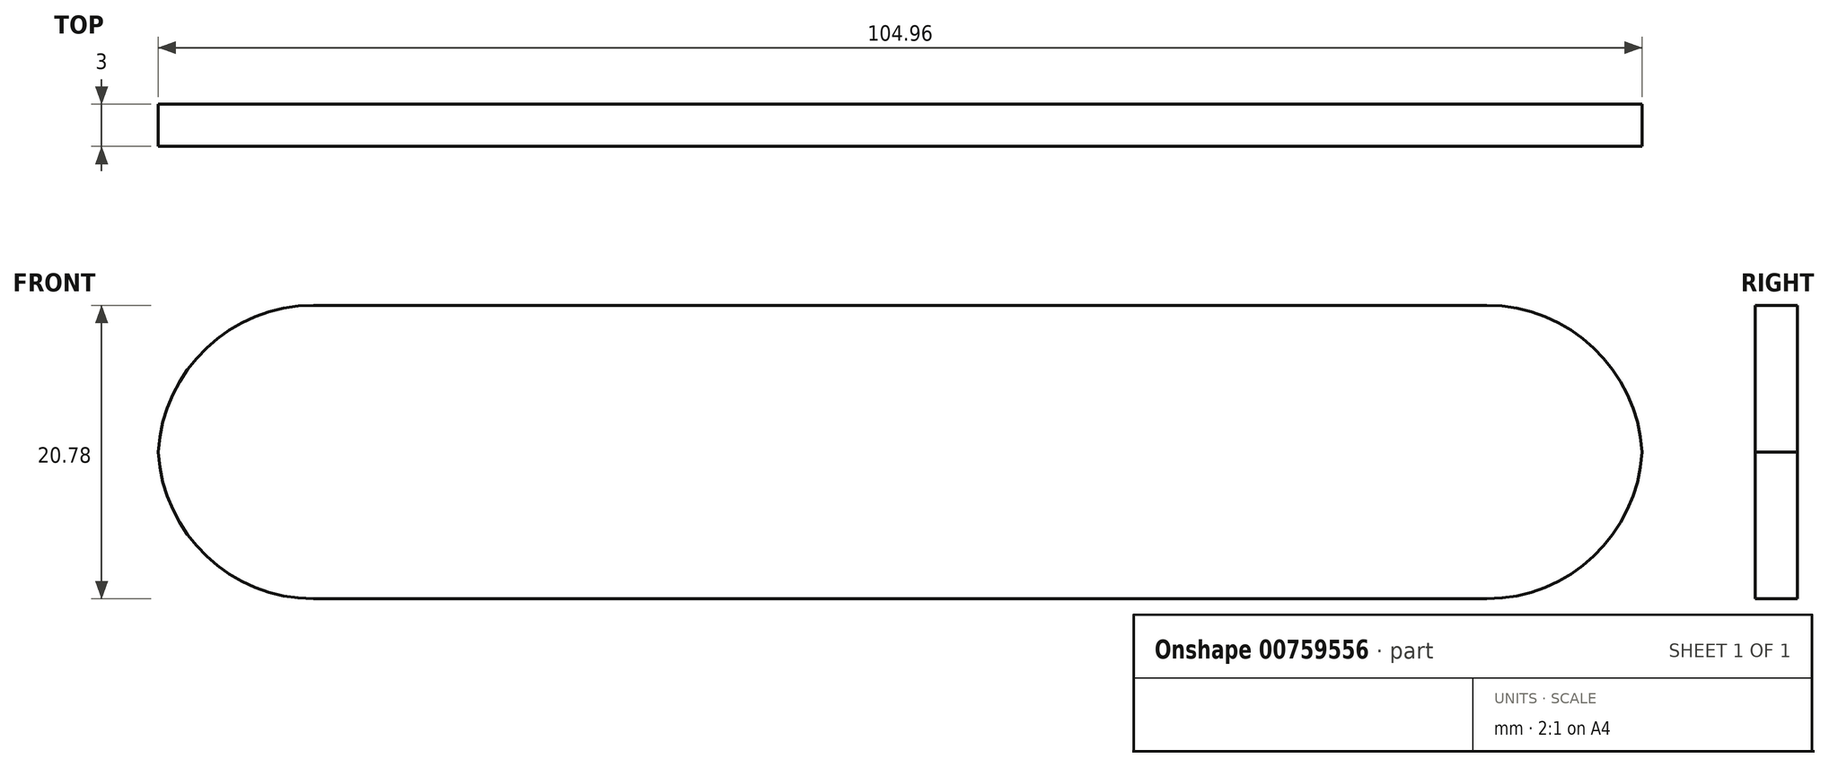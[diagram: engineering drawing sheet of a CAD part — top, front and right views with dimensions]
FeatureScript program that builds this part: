
annotation { "Feature Type Name" : "Feature", "Feature Type Description" : "" }
export const myFeature = defineFeature(function(context is Context, id is Id, definition is map)
    precondition{}
    {
        {
            var Q0;
            Q0=qCreatedBy(makeId("Front.planeOp"),FACE);
            var sketch = newSketch(context, id + "F0", { "sketchPlane" : qUnion([Q0])});
            skLineSegment(sketch, "E0.bottom", {"start": v(52.5, 10.39) * mm, "end": v(-52.5, 10.39) * mm});
            skLineSegment(sketch, "E0.top", {"start": v(52.5, -10.39) * mm, "end": v(-52.5, -10.39) * mm});
            skLineSegment(sketch, "E0.left", {"start": v(52.5, 10.39) * mm, "end": v(52.5, -10.39) * mm});
            skLineSegment(sketch, "E0.right", {"start": v(-52.5, 10.39) * mm, "end": v(-52.5, -10.39) * mm});
            skPoint(sketch, "E0.middle", {"position": v(0, 0) * mm});
            skSolve(sketch);
        }
        {
            var Q0;
            Q0 = qSketchRegion(id + "F0", true);
            extrude(context, id + "F1", {"entities" : qUnion([Q0]), "depth" : 3 * mm, "offsetDistance" : 25 * mm});
        }
        {
            var Q0;
            Q0=makeQuery(id+"F1.opExtrude","SWEPT_EDGE",EDGE,{"disambiguationData":[OSD([sQuery(id+"F0.wireOp",EDGE,"E0.bottom"),sQuery(id+"F0.wireOp",EDGE,"E0.right")])]});
            var Q1;
            Q1=makeQuery(id+"F1.opExtrude","SWEPT_EDGE",EDGE,{"disambiguationData":[OSD([sQuery(id+"F0.wireOp",EDGE,"E0.top"),sQuery(id+"F0.wireOp",EDGE,"E0.right")])]});
            var Q2;
            Q2=makeQuery(id+"F1.opExtrude","SWEPT_EDGE",EDGE,{"disambiguationData":[OSD([sQuery(id+"F0.wireOp",EDGE,"E0.bottom"),sQuery(id+"F0.wireOp",EDGE,"E0.left")])]});
            var Q3;
            Q3=makeQuery(id+"F1.opExtrude","SWEPT_EDGE",EDGE,{"disambiguationData":[OSD([sQuery(id+"F0.wireOp",EDGE,"E0.top"),sQuery(id+"F0.wireOp",EDGE,"E0.left")])]});
            fillet(context, id + "F2", {"entities" : qUnion([Q0, Q1, Q2, Q3]), "radius" : 11 * mm, "tangentPropagation" : true, "allowEdgeOverflow" : false});
        }
    });
